# Revit family: 31790 Контейнерная площадка для ТБО «Сплит» без хозблока Хоббика
name_source: partatom
category: Антураж
revit_build: Autodesk Revit 2018 (Build: 20180423_1000(x64)
units: mm (PartAtom-declared; Revit-internal decimal feet)

## family parameters
Всегда вертикально = Да
Источник визуального образа = Геометрия семейства
На основе рабочей плоскости = Нет
Общий = Нет
При загрузке вырезать с полостями = Нет
Точка расчета площади = Нет

## types (6) — shared parameters
URL = https://hobbyka.ru
Артикул товара = Арт. 31790
Версия 9,47 м = Нет
Высота = 2250 мм
Группа модели = Контейнерные площадки для ТБО
Изготовитель = ООО «Хоббика»
Изображение типоразмера = Контейнерная площадка для ТБО «Сплит» без хозблока Арт 31790.jpg
Материал изделия = Сталь
Цвет каркаса = Сталь
Ширина = 2000 мм

## per-type parameters (varying)
| type | Версия 1,72 м | Версия 3,27 м | Версия 4,82 м | Версия 6,37 м | Версия 7,92 м | Длина | Описание |
| Версия 1,72 м | Да | Нет | Нет | Нет | Нет | 1720 мм | Контейнерная площадка для ТБО «Сплит» без хозблока. Версия 1,72 м |
| Версия 3,27 м | Нет | Да | Нет | Нет | Нет | 3270 мм | Контейнерная площадка для ТБО «Сплит» без хозблока. Версия 3,27 м |
| Версия 4,82 м | Нет | Нет | Да | Нет | Нет | 4820 мм | Контейнерная площадка для ТБО «Сплит» без хозблока. Версия 4,82 м |
| Версия 6,37 м | Нет | Нет | Нет | Да | Нет | 6370 мм | Контейнерная площадка для ТБО «Сплит» без хозблока. Версия 6,37 м |
| Версия 7,92 м | Нет | Нет | Нет | Нет | Да | 7920 мм | Контейнерная площадка для ТБО «Сплит» без хозблока. Версия 7,92 м |
| Версия 9,47 м | Нет | Нет | Нет | Нет | Нет | 9470 мм | Контейнерная площадка для ТБО «Сплит» без хозблока. Версия 9,47 м |
